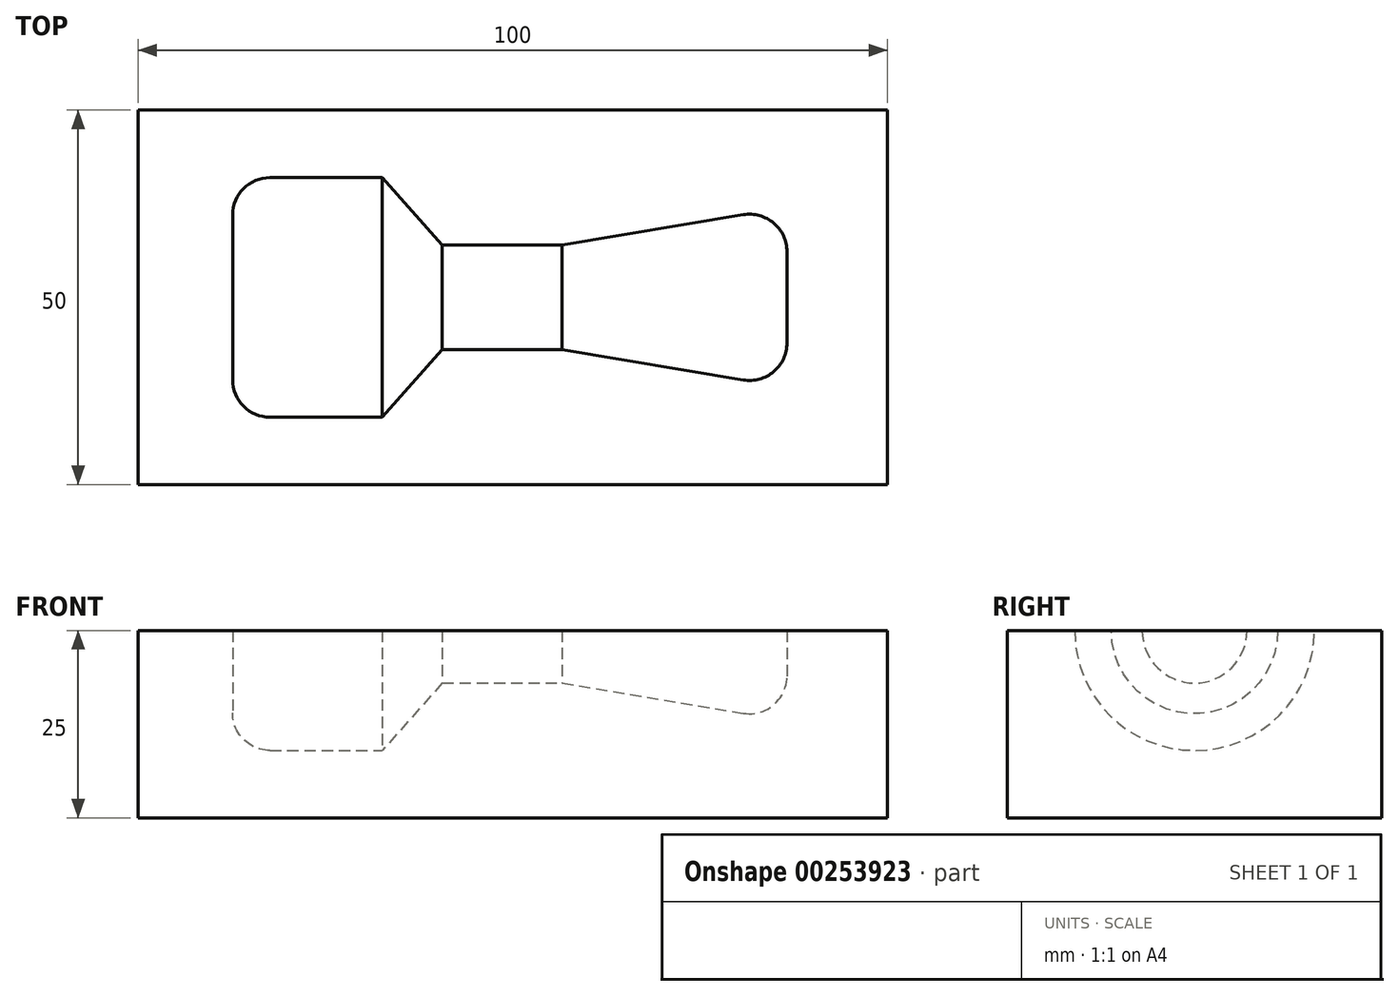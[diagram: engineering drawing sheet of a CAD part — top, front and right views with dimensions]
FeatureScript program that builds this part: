
annotation { "Feature Type Name" : "Feature", "Feature Type Description" : "" }
export const myFeature = defineFeature(function(context is Context, id is Id, definition is map)
    precondition{}
    {
        {
            var Q0;
            Q0=qCreatedBy(makeId("Top.planeOp"),FACE);
            var sketch = newSketch(context, id + "F0", { "sketchPlane" : qUnion([Q0])});
            skLineSegment(sketch, "E0.bottom", {"start": v(50, -25) * mm, "end": v(-50, -25) * mm});
            skLineSegment(sketch, "E0.top", {"start": v(50, 25) * mm, "end": v(-50, 25) * mm});
            skLineSegment(sketch, "E0.left", {"start": v(50, -25) * mm, "end": v(50, 25) * mm});
            skLineSegment(sketch, "E0.right", {"start": v(-50, -25) * mm, "end": v(-50, 25) * mm});
            skPoint(sketch, "E0.middle", {"position": v(0, 0) * mm});
            skSolve(sketch);
        }
        {
            var Q0;
            Q0=makeQuery(id+"F0.imprint","IMPRINT",FACE,{"disambiguationData":[TD([[makeQuery(id+"F0.imprint","IMPRINT",EDGE,{"derivedFrom":sQuery(id+"F0.wireOp",EDGE,"E0.bottom")}),-1.0]])]});
            extrude(context, id + "F1", {"entities" : qUnion([Q0]), "depth" : 25 * mm});
        }
        {
            var Q0;
            Q0=makeQuery(id+"F1.opExtrude","CAP_FACE",FACE,{"disambiguationData":[OSD([sQuery(id+"F0.wireOp",EDGE,"E0.bottom"),sQuery(id+"F0.wireOp",EDGE,"E0.top"),sQuery(id+"F0.wireOp",EDGE,"E0.left"),sQuery(id+"F0.wireOp",EDGE,"E0.right")])],"isStart":false});
            var sketch = newSketch(context, id + "F2", { "sketchPlane" : qUnion([Q0])});
            skLineSegment(sketch, "E1", {"start": v(-32.4, 16) * mm, "end": v(-17.4, 16) * mm});
            skLineSegment(sketch, "E2", {"start": v(-17.4, 16) * mm, "end": v(-9.4, 7) * mm});
            skLineSegment(sketch, "E3", {"start": v(-9.4, 7) * mm, "end": v(6.6, 7) * mm});
            skLineSegment(sketch, "E4", {"start": v(6.6, 7) * mm, "end": v(30.78, 11.03) * mm});
            skLineSegment(sketch, "E5", {"start": v(36.6, 6.1) * mm, "end": v(36.6, 0) * mm});
            skLineSegment(sketch, "E6", {"start": v(-37.4, 0) * mm, "end": v(-37.4, 11) * mm});
            skPoint(sketch, "E7.visualSharp", {"position": v(-37.4, 16) * mm});
            skArc(sketch, "E7.filletArc", {"start": v(-32.4, 16) * mm, "mid": v(-35.94, 14.54) * mm, "end": v(-37.4, 11) * mm});
            skPoint(sketch, "E8.visualSharp", {"position": v(-37.4, -16) * mm});
            skPoint(sketch, "E9.visualSharp", {"position": v(36.6, 12) * mm});
            skArc(sketch, "E9.filletArc", {"start": v(36.6, 6.1) * mm, "mid": v(34.83, 9.91) * mm, "end": v(30.78, 11.03) * mm});
            skPoint(sketch, "E10.visualSharp", {"position": v(36.6, -12) * mm});
            skLineSegment(sketch, "E11", {"start": v(-40.55, 0) * mm, "end": v(42.78, 0) * mm});
            skPoint(sketch, "E12.end.orphan", {"position": v(-17.4, -16) * mm});
            skPoint(sketch, "E13.end.orphan", {"position": v(-9.4, -7) * mm});
            skPoint(sketch, "E14.end.orphan", {"position": v(6.6, -7) * mm});
            skSolve(sketch);
        }
        {
            var Q0;
            Q0=makeQuery(id+"F2.imprint","IMPRINT",FACE,{"disambiguationData":[TD([[makeQuery(id+"F2.imprint","IMPRINT",EDGE,{"derivedFrom":sQuery(id+"F2.wireOp",EDGE,"E1")}),-1.0]])]});
            var Q1;
            Q1=sQuery(id+"F2.wireOp",EDGE,"E11");
            revolve(context, id + "F3", {"operationType" : NewBodyOperationType.REMOVE, "entities" : qUnion([Q0]), "axis" : qUnion([Q1]), "revolveType" : RevolveType.FULL, "oppositeDirection" : true});
        }
    });
